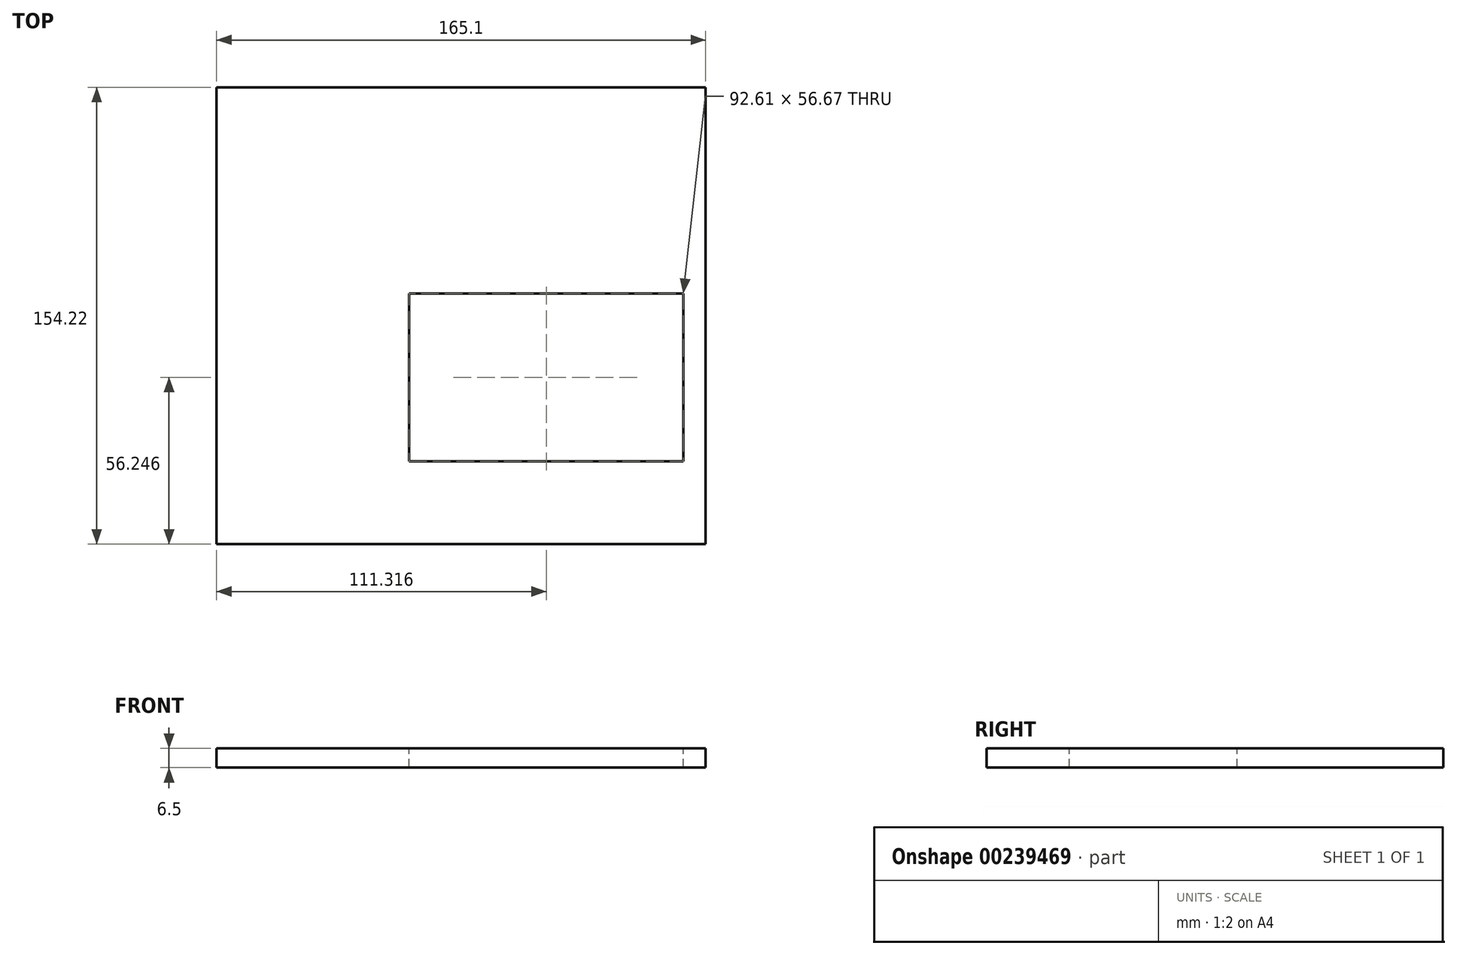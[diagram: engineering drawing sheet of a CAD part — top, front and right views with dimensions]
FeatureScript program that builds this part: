
annotation { "Feature Type Name" : "Feature", "Feature Type Description" : "" }
export const myFeature = defineFeature(function(context is Context, id is Id, definition is map)
    precondition{}
    {
        {
            assignVariable(context, id + "F0", {"name" : "J", "anyValue" : 6.5});
        }
        {
            var Q0;
            Q0=qCreatedBy(makeId("Top.planeOp"),FACE);
            var sketch = newSketch(context, id + "F1", { "sketchPlane" : qUnion([Q0])});
            skLineSegment(sketch, "E0.bottom", {"start": v(-82.55, 77.11) * mm, "end": v(82.55, 77.11) * mm});
            skLineSegment(sketch, "E0.top", {"start": v(-82.55, -77.11) * mm, "end": v(82.55, -77.11) * mm});
            skLineSegment(sketch, "E0.left", {"start": v(-82.55, 77.11) * mm, "end": v(-82.55, -77.11) * mm});
            skLineSegment(sketch, "E0.right", {"start": v(82.55, 77.11) * mm, "end": v(82.55, -77.11) * mm});
            skPoint(sketch, "E0.middle", {"position": v(0, 0) * mm});
            skSolve(sketch);
        }
        {
            var Q0;
            Q0 = qSketchRegion(id + "F1", true);
            extrude(context, id + "F2", {"entities" : qUnion([Q0]), "depth" : (getVariable(context, 'J')) * mm});
        }
        {
            var Q0;
            Q0=makeQuery(id+"F2.opExtrude","SWEPT_FACE",FACE,{"disambiguationData":[OSD([sQuery(id+"F1.wireOp",EDGE,"E0.right")])]});
            var sketch = newSketch(context, id + "F3", { "sketchPlane" : qUnion([Q0])});
            skCircle(sketch, "E1", {"center": v(-12.2, 81.32) * mm, "radius": 27.65 * mm});
            skSolve(sketch);
        }
        {
            var Q0;
            Q0 = qSketchRegion(id + "F3", true);
            extrude(context, id + "F4", {"entities" : qUnion([Q0]), "operationType" : NewBodyOperationType.REMOVE, "oppositeDirection" : true, "depth" : 247.4 * mm});
        }
        {
            var Q0;
            Q0=makeQuery(id+"F2.opExtrude","CAP_FACE",FACE,{"disambiguationData":[OSD([sQuery(id+"F1.wireOp",EDGE,"E0.bottom"),sQuery(id+"F1.wireOp",EDGE,"E0.top"),sQuery(id+"F1.wireOp",EDGE,"E0.left"),sQuery(id+"F1.wireOp",EDGE,"E0.right")])],"isStart":false});
            var sketch = newSketch(context, id + "F5", { "sketchPlane" : qUnion([Q0])});
            skLineSegment(sketch, "E2.bottom", {"start": v(-17.54, 7.47) * mm, "end": v(75.07, 7.47) * mm});
            skLineSegment(sketch, "E2.top", {"start": v(-17.54, -49.2) * mm, "end": v(75.07, -49.2) * mm});
            skLineSegment(sketch, "E2.left", {"start": v(-17.54, 7.47) * mm, "end": v(-17.54, -49.2) * mm});
            skLineSegment(sketch, "E2.right", {"start": v(75.07, 7.47) * mm, "end": v(75.07, -49.2) * mm});
            skPoint(sketch, "E2.middle", {"position": v(28.77, -20.86) * mm});
            skSolve(sketch);
        }
        {
            var Q0;
            Q0 = qSketchRegion(id + "F5", true);
            extrude(context, id + "F6", {"entities" : qUnion([Q0]), "operationType" : NewBodyOperationType.REMOVE, "oppositeDirection" : true, "depth" : 25.4 * mm});
        }
    });
